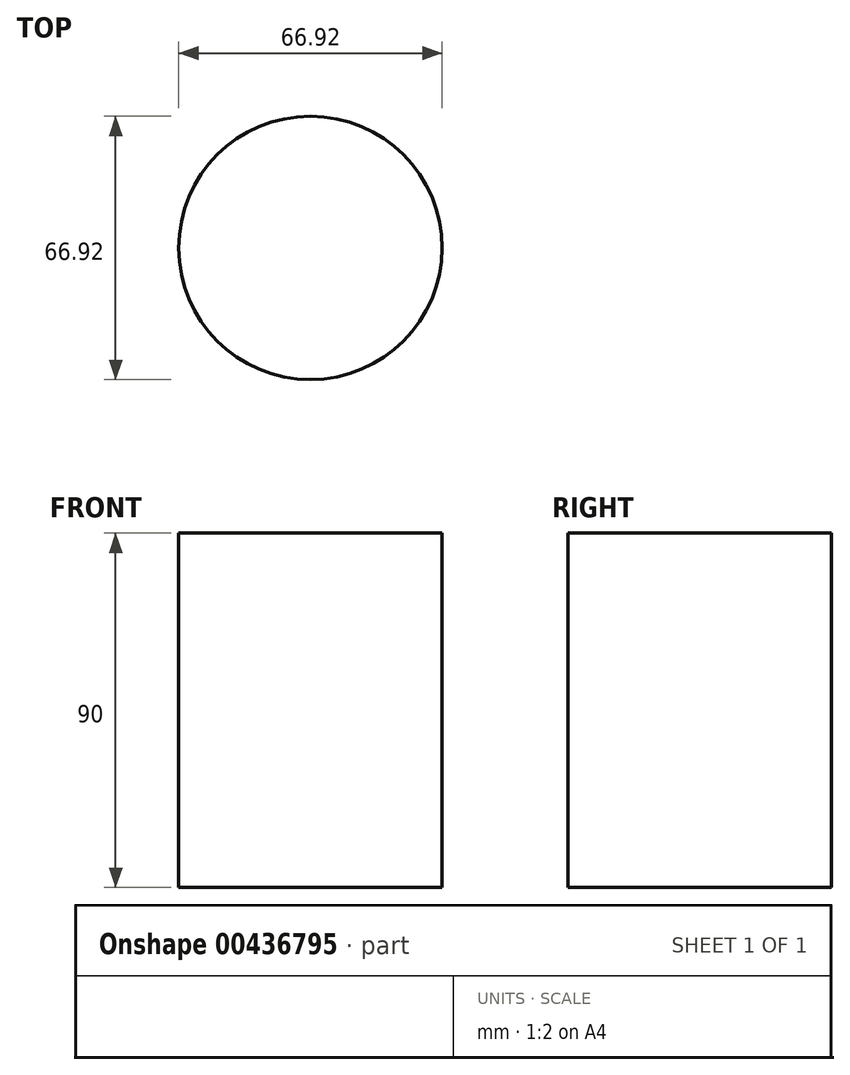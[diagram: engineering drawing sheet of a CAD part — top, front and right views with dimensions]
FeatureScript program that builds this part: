
annotation { "Feature Type Name" : "Feature", "Feature Type Description" : "" }
export const myFeature = defineFeature(function(context is Context, id is Id, definition is map)
    precondition{}
    {
        {
            var Q0;
            Q0=qCreatedBy(makeId("Top.planeOp"),FACE);
            var sketch = newSketch(context, id + "F0", { "sketchPlane" : qUnion([Q0])});
            skCircle(sketch, "E0", {"center": v(0, 0) * mm, "radius": 33.46 * mm});
            skPoint(sketch, "E1", {"position": v(0, -33.46) * mm});
            skSolve(sketch);
        }
        {
            var Q0;
            Q0 = qSketchRegion(id + "F0", true);
            extrude(context, id + "F1", {"entities" : qUnion([Q0]), "depth" : 90 * mm});
        }
    });
